# Revit family: НЕВАТОМ_Клапан КО_20220407
name_source: partatom
category: Арматура воздуховодов
revit_build: Autodesk Revit 2017 (Build: 20170118_1100(x64)
units: mm (PartAtom-declared; Revit-internal decimal feet)

## family parameters
Всегда вертикально = Нет
На основе рабочей плоскости = Нет
Общий = Нет
При загрузке вырезать с полостями = Нет
Размер круглого соединителя = Использовать диаметр
Тип детали = Вставляется

## types (15) — shared parameters
200 = 200 мм
50 = 50 мм
ADSK_Единица измерения = шт.
ADSK_Завод-изготовитель = NEVATOM
ADSK_Масса_Текст = кг
ADSK_Материал наименование = Оцинкованная сталь
ADSK_Наименование = КЛАПАН ОБРАТНЫЙ
ADSK_Напряжение = 0 В
ADSK_Полная мощность = 0 В·А
ADSK_Размер_Ширина = 200 мм
ADSK_Ток = 0 А
Nevatom_URL = https://t.me
d = 10 мм
n = 6
t = 1 мм
Закрыто = Да
Материал корпуса = Материал корпуса
Открыто = Да
zero-valued in all types: ADSK_Масса

## per-type parameters (varying)
| type | ADSK_Размер_Высота | ADSK_Размер_Длина | D | D1 | D2 | Dt | откр |
| КО Ø 160 | 220 мм | 220 мм | 160 мм | 190 мм | 220 мм | 162 мм | 16 мм |
| КО Ø 200 | 260 мм | 260 мм | 200 мм | 230 мм | 260 мм | 202 мм | 20 мм |
| КО Ø 250 | 310 мм | 310 мм | 250 мм | 280 мм | 310 мм | 252 мм | 25 мм |
| КО Ø 315 | 375 мм | 375 мм | 315 мм | 345 мм | 375 мм | 317 мм | 32 мм |
| КО Ø 355 | 415 мм | 415 мм | 355 мм | 385 мм | 415 мм | 357 мм | 36 мм |
| КО Ø 400 | 460 мм | 460 мм | 400 мм | 425 мм | 460 мм | 402 мм | 40 мм |
| КО Ø 500 | 560 мм | 560 мм | 500 мм | 525 мм | 560 мм | 502 мм | 50 мм |
| КО Ø 560 | 620 мм | 620 мм | 560 мм | 585 мм | 620 мм | 562 мм | 56 мм |
| КО Ø 630 | 690 мм | 690 мм | 630 мм | 655 мм | 690 мм | 632 мм | 63 мм |
| КО Ø 710 | 790 мм | 790 мм | 710 мм | 742 мм | 790 мм | 712 мм | 71 мм |
| КО Ø 800 | 880 мм | 880 мм | 800 мм | 832 мм | 880 мм | 802 мм | 80 мм |
| КО Ø 900 | 980 мм | 980 мм | 900 мм | 932 мм | 980 мм | 902 мм | 90 мм |
| КО Ø 1000 | 1080 мм | 1080 мм | 1000 мм | 1032 мм | 1080 мм | 1002 мм | 100 мм |
| КО Ø 1120 | 1184 мм | 1184 мм | 1120 мм | 1152 мм | 1184 мм | 1122 мм | 112 мм |
| КО Ø 1250 | 1330 мм | 1330 мм | 1250 мм | 1282 мм | 1330 мм | 1252 мм | 125 мм |

note: column(s) folded — value = type name in every type: ADSK_Марка
